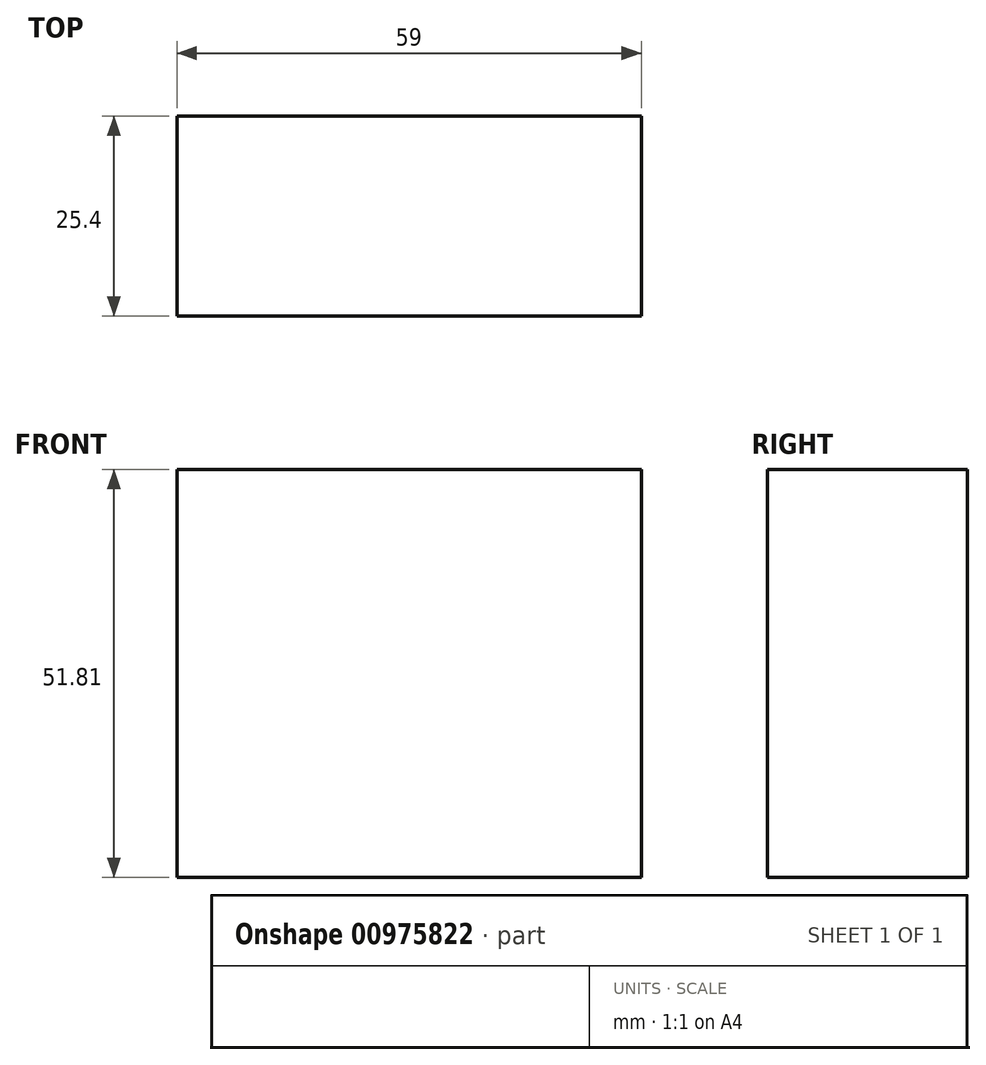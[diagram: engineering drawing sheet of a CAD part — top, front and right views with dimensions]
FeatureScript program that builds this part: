
annotation { "Feature Type Name" : "Feature", "Feature Type Description" : "" }
export const myFeature = defineFeature(function(context is Context, id is Id, definition is map)
    precondition{}
    {
        {
            var Q0;
            Q0=qCreatedBy(makeId("Front.planeOp"),FACE);
            var sketch = newSketch(context, id + "F0", { "sketchPlane" : qUnion([Q0])});
            skLineSegment(sketch, "E0.bottom", {"start": v(-27.77, 27.49) * mm, "end": v(31.23, 27.49) * mm});
            skLineSegment(sketch, "E0.top", {"start": v(-27.77, -24.32) * mm, "end": v(31.23, -24.32) * mm});
            skLineSegment(sketch, "E0.left", {"start": v(-27.77, 27.49) * mm, "end": v(-27.77, -24.32) * mm});
            skLineSegment(sketch, "E0.right", {"start": v(31.23, 27.49) * mm, "end": v(31.23, -24.32) * mm});
            skSolve(sketch);
        }
        {
            var Q0;
            Q0=makeQuery(id+"F0.imprint","IMPRINT",FACE,{"disambiguationData":[TD([[makeQuery(id+"F0.imprint","IMPRINT",EDGE,{"derivedFrom":sQuery(id+"F0.wireOp",EDGE,"E0.bottom")}),-1.0]])]});
            extrude(context, id + "F1", {"entities" : qUnion([Q0]), "depth" : 25.4 * mm, "offsetDistance" : 25.4 * mm});
        }
    });
